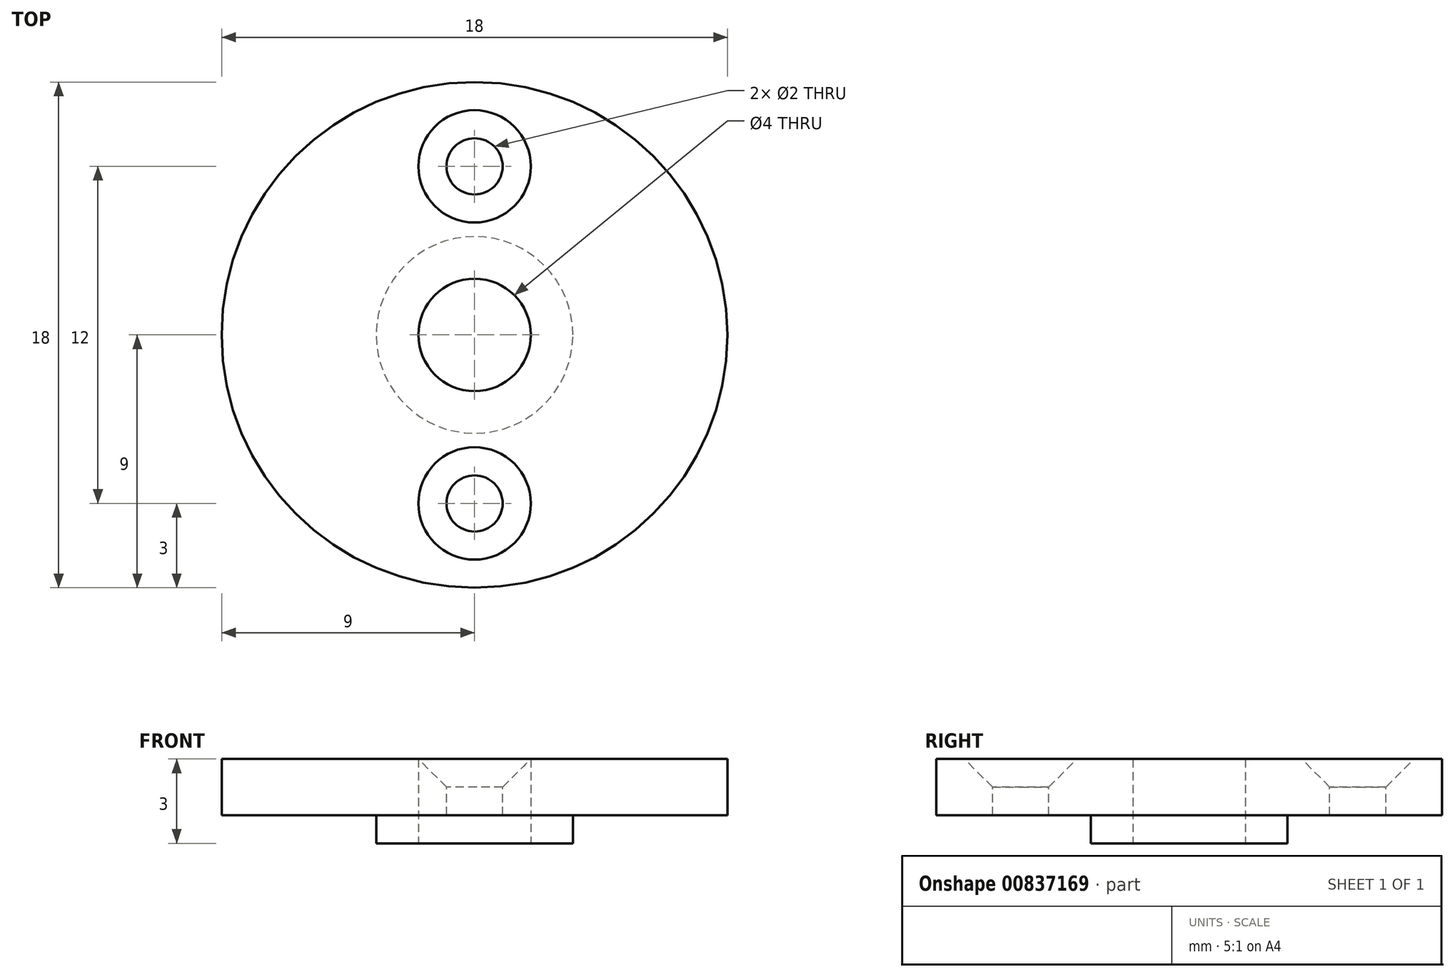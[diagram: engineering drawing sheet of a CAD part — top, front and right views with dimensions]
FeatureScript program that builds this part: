
annotation { "Feature Type Name" : "Feature", "Feature Type Description" : "" }
export const myFeature = defineFeature(function(context is Context, id is Id, definition is map)
    precondition{}
    {
        {
            var Q0;
            Q0=qCreatedBy(makeId("Top.planeOp"),FACE);
            var sketch = newSketch(context, id + "F0", { "sketchPlane" : qUnion([Q0])});
            skCircle(sketch, "E0", {"center": v(0, 0) * mm, "radius": 9 * mm});
            skCircle(sketch, "E1", {"center": v(0, 0) * mm, "radius": 2 * mm});
            skCircle(sketch, "E2", {"center": v(0, 0) * mm, "radius": 3.5 * mm});
            skSolve(sketch);
        }
        {
            var Q0;
            Q0=makeQuery(id+"F0.imprint","IMPRINT",FACE,{"disambiguationData":[TD([[makeQuery(id+"F0.imprint","IMPRINT",EDGE,{"derivedFrom":sQuery(id+"F0.wireOp",EDGE,"E0")}),1.0]])]});
            var Q1;
            Q1=makeQuery(id+"F0.imprint","IMPRINT",FACE,{"disambiguationData":[TD([[makeQuery(id+"F0.imprint","IMPRINT",EDGE,{"derivedFrom":sQuery(id+"F0.wireOp",EDGE,"E1")}),-1.0]])]});
            extrude(context, id + "F1", {"entities" : qUnion([Q0, Q1]), "depth" : 2 * mm, "offsetDistance" : 25 * mm});
        }
        {
            var Q0;
            Q0=makeQuery(id+"F0.imprint","IMPRINT",FACE,{"disambiguationData":[TD([[makeQuery(id+"F0.imprint","IMPRINT",EDGE,{"derivedFrom":sQuery(id+"F0.wireOp",EDGE,"E1")}),-1.0]])]});
            extrude(context, id + "F2", {"entities" : qUnion([Q0]), "operationType" : NewBodyOperationType.ADD, "oppositeDirection" : true, "depth" : 1 * mm, "offsetDistance" : 25 * mm});
        }
        {
            var Q0;
            Q0=makeQuery(id+"F1.opExtrude","CAP_FACE",FACE,{"disambiguationData":[OSD([sQuery(id+"F0.wireOp",EDGE,"E0"),sQuery(id+"F0.wireOp",EDGE,"E1")])],"isStart":false});
            var sketch = newSketch(context, id + "F3", { "sketchPlane" : qUnion([Q0])});
            skLineSegment(sketch, "E3", {"start": v(0, 0) * mm, "end": v(0, -9) * mm, "construction": true});
            skLineSegment(sketch, "E4", {"start": v(0, 0) * mm, "end": v(0, 9) * mm, "construction": true});
            skPoint(sketch, "E5", {"position": v(0, 6) * mm});
            skPoint(sketch, "E6", {"position": v(0, -6) * mm});
            skSolve(sketch);
        }
        {
            var Q0;
            Q0=sQuery(id+"F3.wireOp",VERTEX,"E5");
            var Q1;
            Q1=sQuery(id+"F3.wireOp",VERTEX,"E6");
            var Q2;
            Q2=makeQuery(id+"F1.opExtrude","SWEPT_BODY",BODY,{"disambiguationData":[OSD([sQuery(id+"F0.wireOp",EDGE,"E0"),sQuery(id+"F0.wireOp",EDGE,"E1")])]});
            hole(context, id + "F4", {"style" : HoleStyle.C_SINK, "endStyle" : HoleEndStyle.THROUGH, "holeDiameter" : 2 * mm, "cSinkDiameter" : 4 * mm, "cSinkAngle" : 90 * degree, "majorDiameter" : 5 * mm, "isTappedThrough" : true, "tappedDepth" : 12 * mm, "tapClearance" : 3, "locations" : qUnion([Q0, Q1]), "scope" : qUnion([Q2])});
        }
    });
